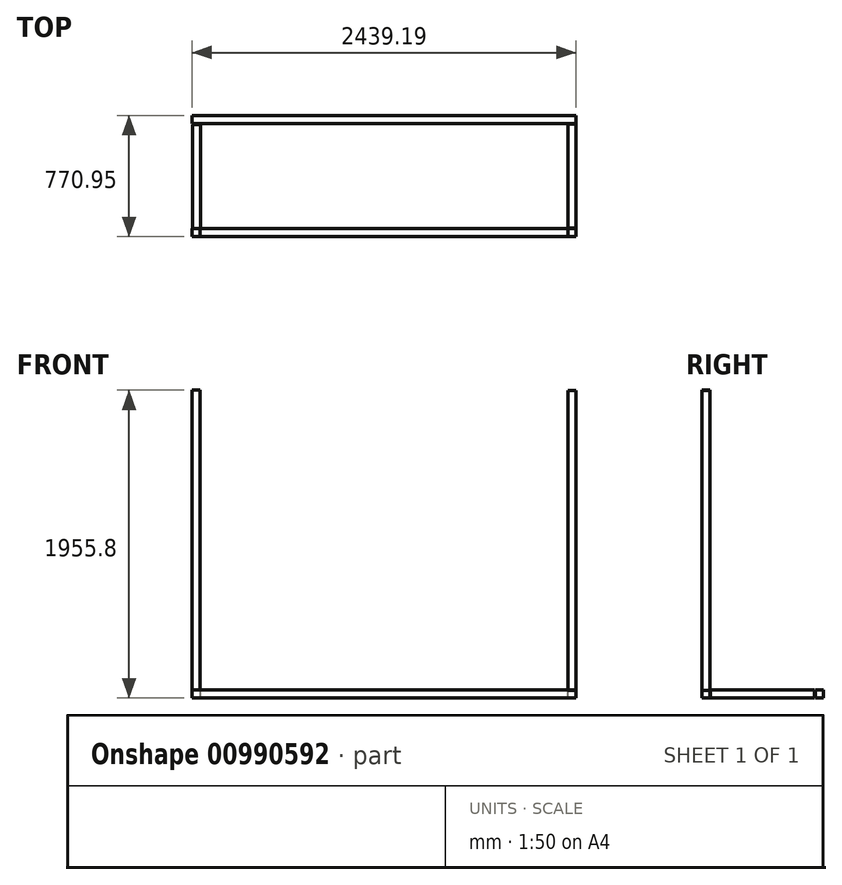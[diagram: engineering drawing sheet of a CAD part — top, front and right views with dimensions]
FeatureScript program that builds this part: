
annotation { "Feature Type Name" : "Feature", "Feature Type Description" : "" }
export const myFeature = defineFeature(function(context is Context, id is Id, definition is map)
    precondition{}
    {
        {
            var Q0;
            Q0=qCreatedBy(makeId("Top.planeOp"),FACE);
            var sketch = newSketch(context, id + "F0", { "sketchPlane" : qUnion([Q0])});
            skLineSegment(sketch, "E0.bottom", {"start": v(-1128.12, 104.4) * mm, "end": v(1310.28, 104.4) * mm});
            skLineSegment(sketch, "E0.top", {"start": v(-1128.12, 155.2) * mm, "end": v(1310.28, 155.2) * mm});
            skLineSegment(sketch, "E0.left", {"start": v(-1128.12, 104.4) * mm, "end": v(-1128.12, 155.2) * mm});
            skLineSegment(sketch, "E0.right", {"start": v(1310.28, 104.4) * mm, "end": v(1310.28, 155.2) * mm});
            skLineSegment(sketch, "E1.bottom", {"start": v(-1128.82, -615.75) * mm, "end": v(1309.58, -615.75) * mm});
            skLineSegment(sketch, "E1.top", {"start": v(-1128.82, -564.95) * mm, "end": v(1309.58, -564.95) * mm});
            skLineSegment(sketch, "E1.left", {"start": v(-1128.82, -615.75) * mm, "end": v(-1128.82, -564.95) * mm});
            skLineSegment(sketch, "E1.right", {"start": v(1309.58, -615.75) * mm, "end": v(1309.58, -564.95) * mm});
            skLineSegment(sketch, "E2.bottom", {"start": v(-1126.8, 97.4) * mm, "end": v(-1076, 97.4) * mm});
            skLineSegment(sketch, "E2.top", {"start": v(-1126.8, -563) * mm, "end": v(-1076, -563) * mm});
            skLineSegment(sketch, "E2.left", {"start": v(-1126.8, 97.4) * mm, "end": v(-1126.8, -563) * mm});
            skLineSegment(sketch, "E2.right", {"start": v(-1076, 97.4) * mm, "end": v(-1076, -563) * mm});
            skLineSegment(sketch, "E3.bottom", {"start": v(1259.36, 99.33) * mm, "end": v(1310.16, 99.33) * mm});
            skLineSegment(sketch, "E3.top", {"start": v(1259.36, -561.07) * mm, "end": v(1310.16, -561.07) * mm});
            skLineSegment(sketch, "E3.left", {"start": v(1259.36, 99.33) * mm, "end": v(1259.36, -561.07) * mm});
            skLineSegment(sketch, "E3.right", {"start": v(1310.16, 99.33) * mm, "end": v(1310.16, -561.07) * mm});
            skSolve(sketch);
        }
        {
            var Q0;
            Q0=sQuery(id+"F0.wireOp",EDGE,"E0.top");
            var Q1;
            Q1=sQuery(id+"F0.wireOp",EDGE,"E3.right");
            var Q2;
            Q2=sQuery(id+"F0.wireOp",EDGE,"E1.top");
            var Q3;
            Q3=sQuery(id+"F0.wireOp",EDGE,"E2.left");
            var Q4;
            Q4=sQuery(id+"F0.wireOp",EDGE,"E0.bottom");
            var Q5;
            Q5=sQuery(id+"F0.wireOp",EDGE,"E2.right");
            var Q6;
            Q6=sQuery(id+"F0.wireOp",EDGE,"E1.bottom");
            var Q7;
            Q7=sQuery(id+"F0.wireOp",EDGE,"E3.left");
            var Q8;
            Q8=sQuery(id+"F0.wireOp",EDGE,"E0.right");
            var Q9;
            Q9=sQuery(id+"F0.wireOp",EDGE,"E0.left");
            var Q10;
            Q10=sQuery(id+"F0.wireOp",EDGE,"E1.left");
            var Q11;
            Q11=sQuery(id+"F0.wireOp",EDGE,"E3.top");
            var Q12;
            Q12=sQuery(id+"F0.wireOp",EDGE,"E2.bottom");
            var Q13;
            Q13=sQuery(id+"F0.wireOp",EDGE,"E3.bottom");
            var Q14;
            Q14=sQuery(id+"F0.wireOp",EDGE,"E1.right");
            var Q15;
            Q15=sQuery(id+"F0.wireOp",EDGE,"E2.top");
            extrude(context, id + "F1", {"bodyType" : ToolBodyType.SURFACE, "surfaceEntities" : qUnion([Q0, Q1, Q2, Q3, Q4, Q5, Q6, Q7, Q8, Q9, Q10, Q11, Q12, Q13, Q14, Q15]), "depth" : 50.8 * mm, "offsetDistance" : 25.4 * mm});
        }
        {
            var Q0;
            Q0=makeQuery(id+"F1.opExtrude","SWEPT_FACE",FACE,{"disambiguationData":[OSD([sQuery(id+"F0.wireOp",EDGE,"E1.bottom")])]});
            var sketch = newSketch(context, id + "F2", { "sketchPlane" : qUnion([Q0])});
            skLineSegment(sketch, "E4.bottom", {"start": v(1128.82, 50.8) * mm, "end": v(1078.02, 50.8) * mm});
            skLineSegment(sketch, "E4.top", {"start": v(1128.82, 1955.8) * mm, "end": v(1078.02, 1955.8) * mm});
            skLineSegment(sketch, "E4.left", {"start": v(1128.82, 50.8) * mm, "end": v(1128.82, 1955.8) * mm});
            skLineSegment(sketch, "E4.right", {"start": v(1078.02, 50.8) * mm, "end": v(1078.02, 1955.8) * mm});
            skLineSegment(sketch, "E5.bottom", {"start": v(-1259.57, 50.63) * mm, "end": v(-1310.37, 50.63) * mm});
            skLineSegment(sketch, "E5.top", {"start": v(-1259.57, 1955.63) * mm, "end": v(-1310.37, 1955.63) * mm});
            skLineSegment(sketch, "E5.left", {"start": v(-1259.57, 50.63) * mm, "end": v(-1259.57, 1955.63) * mm});
            skLineSegment(sketch, "E5.right", {"start": v(-1310.37, 50.63) * mm, "end": v(-1310.37, 1955.63) * mm});
            skSolve(sketch);
        }
        {
            var Q0;
            Q0=sQuery(id+"F2.wireOp",EDGE,"E4.left");
            var Q1;
            Q1=sQuery(id+"F2.wireOp",EDGE,"E4.right");
            var Q2;
            Q2=sQuery(id+"F2.wireOp",EDGE,"E5.left");
            var Q3;
            Q3=sQuery(id+"F2.wireOp",EDGE,"E5.right");
            var Q4;
            Q4=sQuery(id+"F2.wireOp",EDGE,"E4.top");
            var Q5;
            Q5=sQuery(id+"F2.wireOp",EDGE,"E5.bottom");
            var Q6;
            Q6=sQuery(id+"F2.wireOp",EDGE,"E4.bottom");
            var Q7;
            Q7=sQuery(id+"F2.wireOp",EDGE,"E5.top");
            extrude(context, id + "F3", {"bodyType" : ToolBodyType.SURFACE, "surfaceEntities" : qUnion([Q0, Q1, Q2, Q3, Q4, Q5, Q6, Q7]), "depth" : 50.8 * mm, "offsetDistance" : 25.4 * mm});
        }
    });
